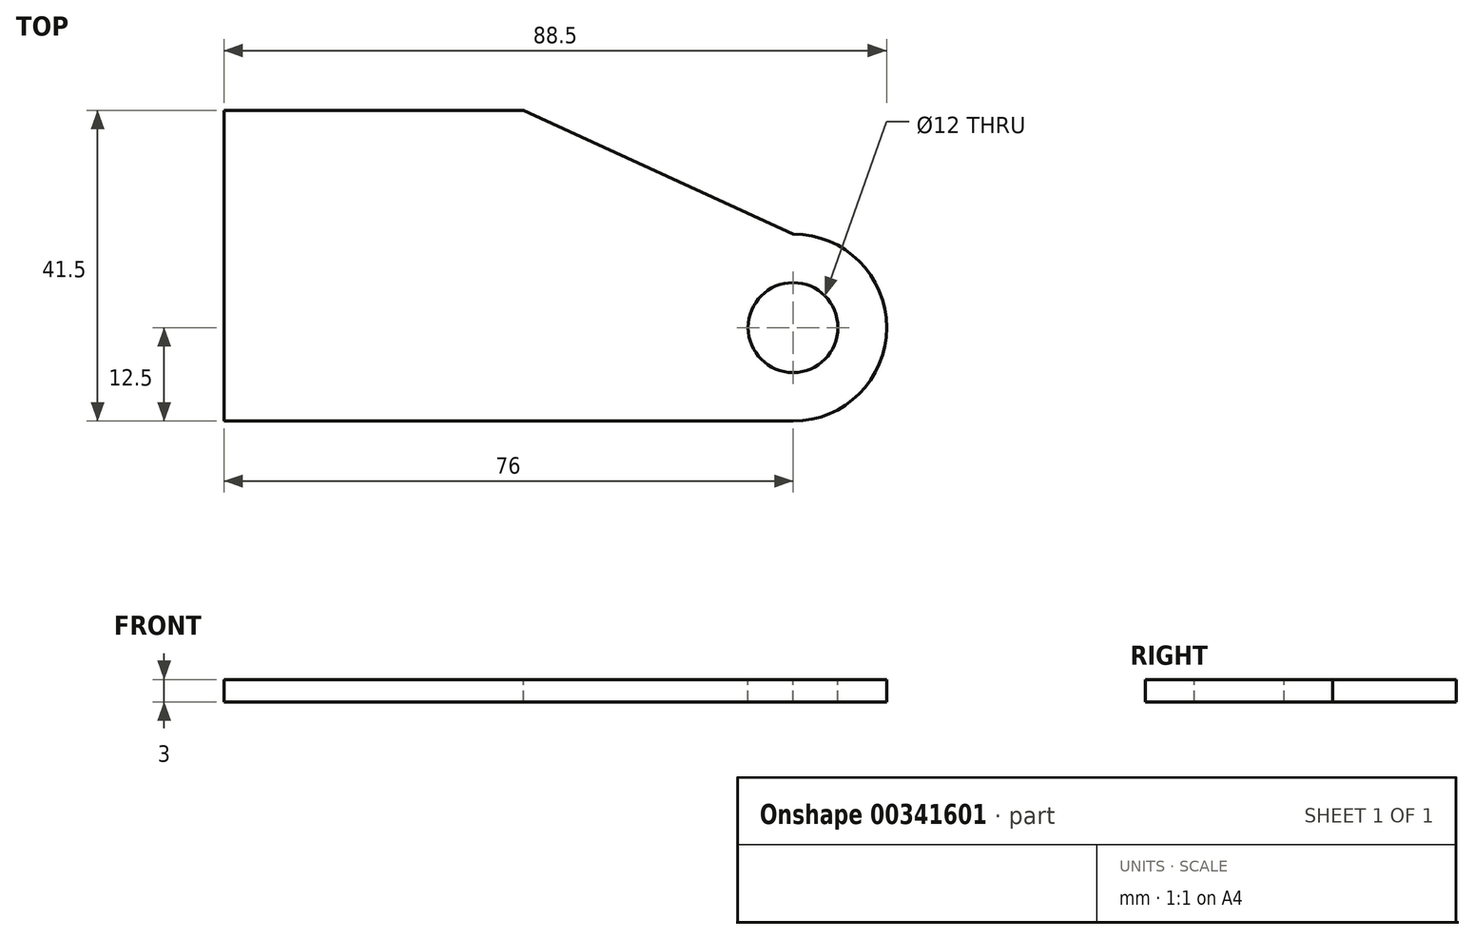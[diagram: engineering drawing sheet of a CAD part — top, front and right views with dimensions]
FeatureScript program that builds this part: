
annotation { "Feature Type Name" : "Feature", "Feature Type Description" : "" }
export const myFeature = defineFeature(function(context is Context, id is Id, definition is map)
    precondition{}
    {
        {
            var Q0;
            Q0=qCreatedBy(makeId("Top.planeOp"),FACE);
            var sketch = newSketch(context, id + "F0", { "sketchPlane" : qUnion([Q0])});
            skLineSegment(sketch, "E0.bottom", {"start": v(-76, 29) * mm, "end": v(-36, 29) * mm});
            skCircle(sketch, "E1", {"center": v(0, 0) * mm, "radius": 6 * mm});
            skLineSegment(sketch, "E2", {"start": v(-36, 29) * mm, "end": v(0, 12.5) * mm});
            skLineSegment(sketch, "E3", {"start": v(0, -12.5) * mm, "end": v(-76, -12.5) * mm});
            skPoint(sketch, "E3.startSnap0", {"position": v(0, -6) * mm});
            skLineSegment(sketch, "E4", {"start": v(-76, 29) * mm, "end": v(-76, -12.5) * mm});
            skArc(sketch, "E5", {"start": v(0, -12.5) * mm, "mid": v(12.5, 0) * mm, "end": v(0, 12.5) * mm});
            skSolve(sketch);
        }
        {
            var Q0;
            Q0=makeQuery(id+"F0.imprint","IMPRINT",FACE,{"disambiguationData":[TD([[makeQuery(id+"F0.imprint","IMPRINT",EDGE,{"derivedFrom":sQuery(id+"F0.wireOp",EDGE,"E0.right")}),1.0]])]});
            var Q1;
            Q1=makeQuery(id+"F0.imprint","IMPRINT",FACE,{"disambiguationData":[TD([[makeQuery(id+"F0.imprint","IMPRINT",EDGE,{"derivedFrom":sQuery(id+"F0.wireOp",EDGE,"E0.bottom")}),-1.0]])]});
            var Q2;
            Q2=makeQuery(id+"F0.imprint","IMPRINT",FACE,{"disambiguationData":[TD([[makeQuery(id+"F0.imprint","IMPRINT",EDGE,{"derivedFrom":sQuery(id+"F0.wireOp",EDGE,"pZG7QtaC-g7sj-Xlo3-LHLi-HS1tBn4Tb0Q1.bottom")}),1.0]])]});
            var Q3;
            {var subQ5=sQuery(id+"F0.wireOp",EDGE,"AhltfCl1-yLZr-sPHS-8FeB-1zx7OxLGBwaN.left");var subQ7=sQuery(id+"F0.wireOp",EDGE,"AhltfCl1-yLZr-sPHS-8FeB-1zx7OxLGBwaN.bottom");var subQ10=makeQuery(id+"F0.imprint","INTERSECT",VERTEX,{"derivedFrom":[subQ7,subQ5]});Q3=makeQuery(id+"F0.imprint","IMPRINT",FACE,{"disambiguationData":[TD([[makeQuery(id+"F0.imprint","IMPRINT",EDGE,{"disambiguationData":[TD([[subQ10,-1.0]])],"derivedFrom":subQ7}),1.0]])]});}
            var Q4;
            Q4=makeQuery(id+"F0.imprint","IMPRINT",FACE,{"disambiguationData":[TD([[makeQuery(id+"F0.imprint","IMPRINT",EDGE,{"derivedFrom":sQuery(id+"F0.wireOp",EDGE,"E1")}),-1.0]])]});
            extrude(context, id + "F1", {"entities" : qUnion([Q0, Q1, Q2, Q3, Q4]), "oppositeDirection" : true, "depth" : 3 * mm});
        }
    });
